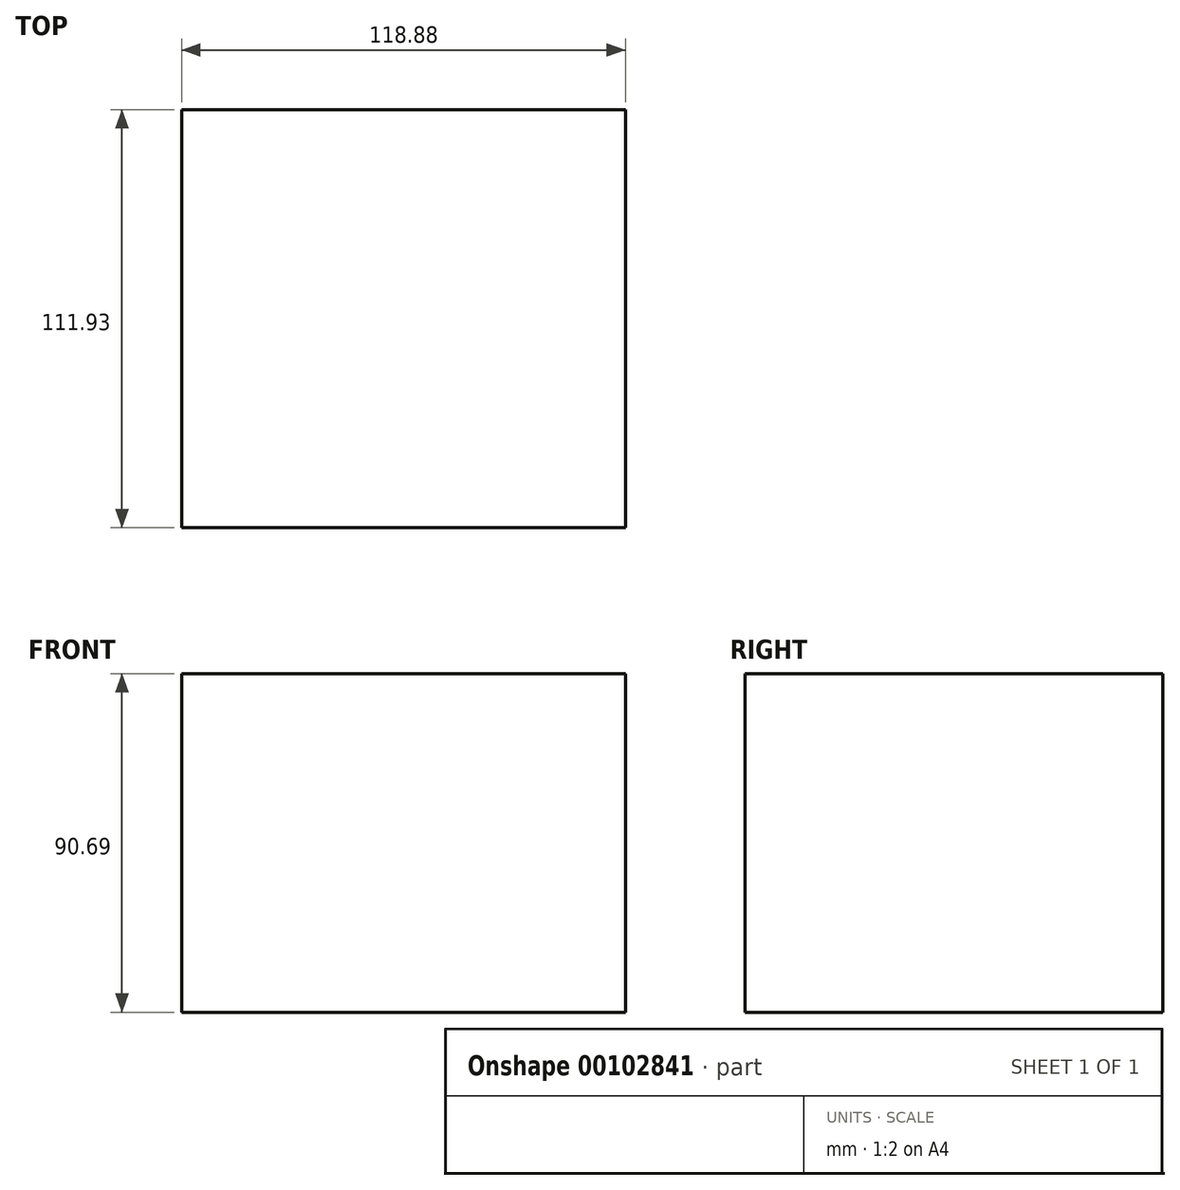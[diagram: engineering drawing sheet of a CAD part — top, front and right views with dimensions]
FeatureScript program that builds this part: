
annotation { "Feature Type Name" : "Feature", "Feature Type Description" : "" }
export const myFeature = defineFeature(function(context is Context, id is Id, definition is map)
    precondition{}
    {
        {
            var Q0;
            Q0=qCreatedBy(makeId("Front.planeOp"),FACE);
            var sketch = newSketch(context, id + "F0", { "sketchPlane" : qUnion([Q0])});
            skLineSegment(sketch, "E0.bottom", {"start": v(-118.88, 37.37) * mm, "end": v(0, 37.37) * mm});
            skLineSegment(sketch, "E0.top", {"start": v(-118.88, -53.32) * mm, "end": v(0, -53.32) * mm});
            skLineSegment(sketch, "E0.left", {"start": v(-118.88, 37.37) * mm, "end": v(-118.88, -53.32) * mm});
            skLineSegment(sketch, "E0.right", {"start": v(0, 37.37) * mm, "end": v(0, -53.32) * mm});
            skSolve(sketch);
        }
        {
            var Q0;
            Q0=makeQuery(id+"F0.imprint","IMPRINT",FACE,{"disambiguationData":[TD([[makeQuery(id+"F0.imprint","IMPRINT",EDGE,{"derivedFrom":sQuery(id+"F0.wireOp",EDGE,"E0.bottom")}),-1.0]])]});
            extrude(context, id + "F1", {"entities" : qUnion([Q0]), "depth" : 111.93 * mm});
        }
    });
